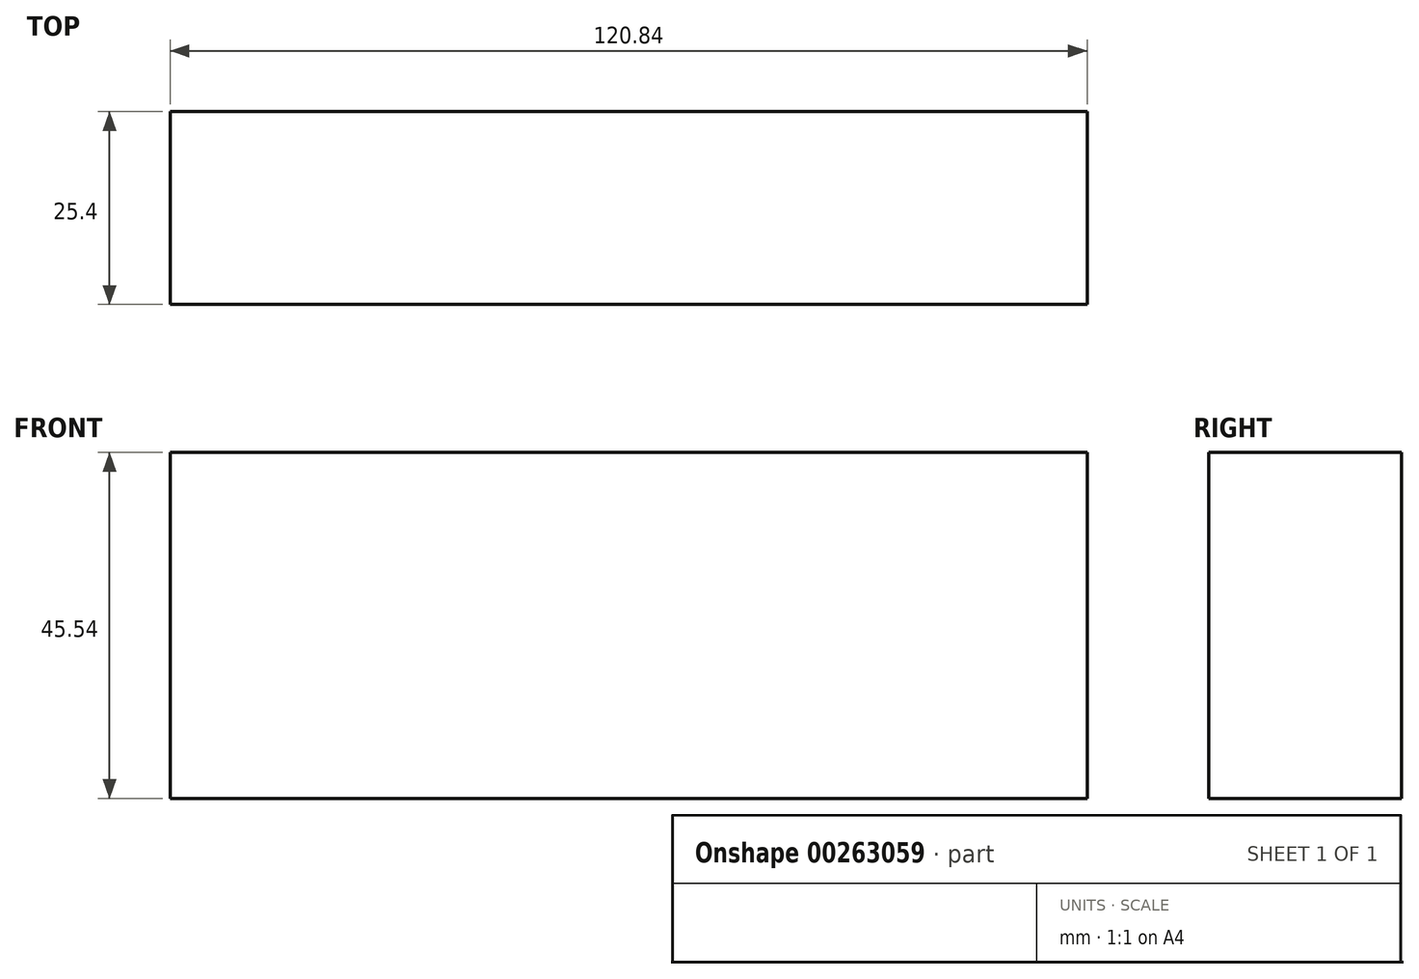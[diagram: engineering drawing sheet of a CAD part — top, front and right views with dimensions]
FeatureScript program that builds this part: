
annotation { "Feature Type Name" : "Feature", "Feature Type Description" : "" }
export const myFeature = defineFeature(function(context is Context, id is Id, definition is map)
    precondition{}
    {
        {
            var Q0;
            Q0=qCreatedBy(makeId("Front.planeOp"),FACE);
            var sketch = newSketch(context, id + "F0", { "sketchPlane" : qUnion([Q0])});
            skLineSegment(sketch, "E0.bottom", {"start": v(-60.42, 22.77) * mm, "end": v(60.42, 22.77) * mm});
            skLineSegment(sketch, "E0.top", {"start": v(-60.42, -22.77) * mm, "end": v(60.42, -22.77) * mm});
            skLineSegment(sketch, "E0.left", {"start": v(-60.42, 22.77) * mm, "end": v(-60.42, -22.77) * mm});
            skLineSegment(sketch, "E0.right", {"start": v(60.42, 22.77) * mm, "end": v(60.42, -22.77) * mm});
            skPoint(sketch, "E0.middle", {"position": v(0, 0) * mm});
            skSolve(sketch);
        }
        {
            var Q0;
            Q0=makeQuery(id+"F0.imprint","IMPRINT",FACE,{"disambiguationData":[TD([[makeQuery(id+"F0.imprint","IMPRINT",EDGE,{"derivedFrom":sQuery(id+"F0.wireOp",EDGE,"E0.bottom")}),-1.0]])]});
            extrude(context, id + "F1", {"entities" : qUnion([Q0]), "depth" : 25.4 * mm});
        }
    });
